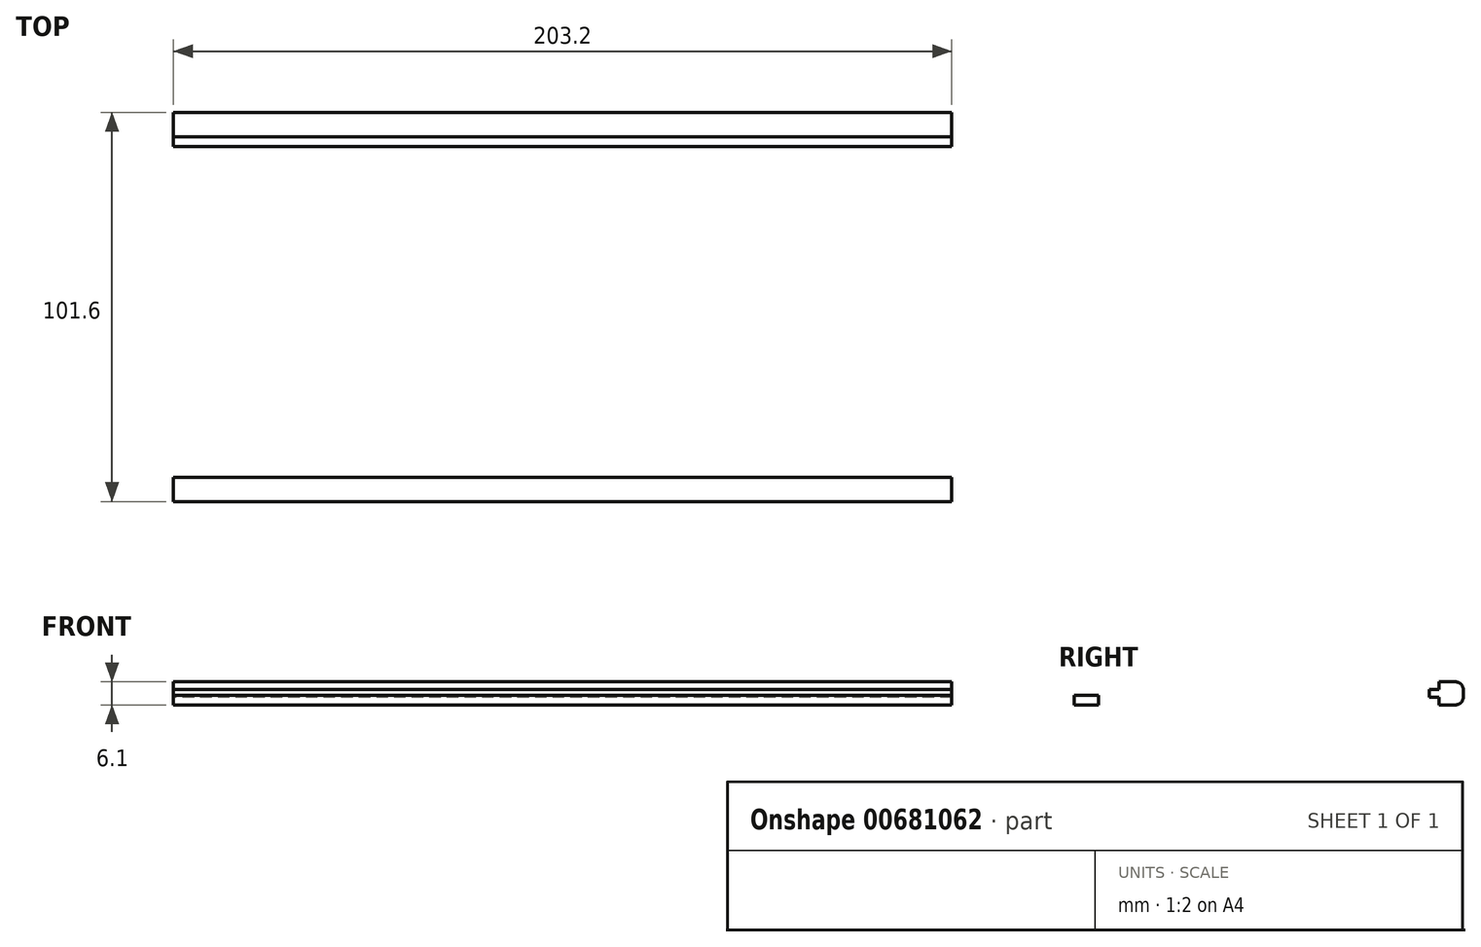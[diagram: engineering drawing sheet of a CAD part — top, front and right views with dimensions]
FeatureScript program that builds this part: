
annotation { "Feature Type Name" : "Feature", "Feature Type Description" : "" }
export const myFeature = defineFeature(function(context is Context, id is Id, definition is map)
    precondition{}
    {
        {
            var Q0;
            Q0=qCreatedBy(makeId("Top.planeOp"),FACE);
            var sketch = newSketch(context, id + "F0", { "sketchPlane" : qUnion([Q0])});
            skLineSegment(sketch, "E0", {"start": v(0, 0) * mm, "end": v(-71.71, 0) * mm});
            skLineSegment(sketch, "E1", {"start": v(71.71, 0) * mm, "end": v(0, 0) * mm});
            skLineSegment(sketch, "E2.bottom", {"start": v(-106, 53.84) * mm, "end": v(97.2, 53.84) * mm});
            skLineSegment(sketch, "E2.top", {"start": v(-106, -47.76) * mm, "end": v(97.2, -47.76) * mm});
            skLineSegment(sketch, "E2.left", {"start": v(-106, 53.84) * mm, "end": v(-106, -47.76) * mm});
            skLineSegment(sketch, "E2.right", {"start": v(97.2, 53.84) * mm, "end": v(97.2, -47.76) * mm});
            skLineSegment(sketch, "E3.top", {"start": v(-106, -41.41) * mm, "end": v(97.2, -41.41) * mm});
            skLineSegment(sketch, "E3.left", {"start": v(-106, -47.76) * mm, "end": v(-106, -41.41) * mm});
            skLineSegment(sketch, "E3.right", {"start": v(97.2, -47.76) * mm, "end": v(97.2, -41.41) * mm});
            skLineSegment(sketch, "E4.top", {"start": v(-106, 47.49) * mm, "end": v(97.2, 47.49) * mm});
            skLineSegment(sketch, "E4.left", {"start": v(-106, 53.84) * mm, "end": v(-106, 47.49) * mm});
            skLineSegment(sketch, "E4.right", {"start": v(97.2, 53.84) * mm, "end": v(97.2, 47.49) * mm});
            skText(sketch, "E5", { "text": "Kira\n", "fontName": "OpenSans-Regular.ttf"});
            const initialGuessF0  = {"E5": [-0.0568, -0.01355, 1, 0, 0.04053]};
            skSetInitialGuess(sketch, initialGuessF0);
            skSolve(sketch);
        }
        {
            var Q0;
            Q0=makeQuery(id+"F0.imprint","IMPRINT",FACE,{"disambiguationData":[TD([[makeQuery(id+"F0.imprint","IMPRINT",EDGE,{"derivedFrom":sQuery(id+"F0.wireOp",EDGE,"E2.bottom")}),-1.0]])]});
            var Q1;
            Q1=makeQuery(id+"F0.imprint","IMPRINT",FACE,{"disambiguationData":[TD([[makeQuery(id+"F0.imprint","IMPRINT",EDGE,{"derivedFrom":sQuery(id+"F0.wireOp",EDGE,"E2.top")}),1.0]])]});
            extrude(context, id + "F1", {"entities" : qUnion([Q0, Q1]), "depth" : 6.1 * mm, "offsetDistance" : 25.4 * mm});
        }
        {
            var Q0;
            Q0=makeQuery(id+"F0.imprint","IMPRINT",FACE,{"disambiguationData":[TD([[makeQuery(id+"F0.imprint","IMPRINT",EDGE,{"derivedFrom":sQuery(id+"F0.wireOp",EDGE,"E2.left")}),1.0]])]});
            extrude(context, id + "F2", {"entities" : qUnion([Q0]), "depth" : 2.54 * mm, "offsetDistance" : 25.4 * mm});
        }
        {
            var Q0;
            Q0=makeQuery(id+"F1.opExtrude","SWEPT_FACE",FACE,{"disambiguationData":[OSD([sQuery(id+"F0.wireOp",EDGE,"E4.top")])]});
            var sketch = newSketch(context, id + "F3", { "sketchPlane" : qUnion([Q0])});
            skLineSegment(sketch, "E6", {"start": v(-106, 4) * mm, "end": v(97.2, 4) * mm});
            skLineSegment(sketch, "E7", {"start": v(97.2, 4) * mm, "end": v(97.2, 2.04) * mm});
            skLineSegment(sketch, "E8", {"start": v(97.2, 2.04) * mm, "end": v(-48.8, 2.04) * mm});
            skLineSegment(sketch, "E9", {"start": v(-48.8, 2.04) * mm, "end": v(-106, 2.04) * mm});
            skLineSegment(sketch, "E10", {"start": v(-106, 2.04) * mm, "end": v(-106, 4) * mm});
            skSolve(sketch);
        }
        {
            var Q0;
            Q0=makeQuery(id+"F3.imprint","IMPRINT",FACE,{"disambiguationData":[TD([[makeQuery(id+"F3.imprint","IMPRINT",EDGE,{"derivedFrom":sQuery(id+"F3.wireOp",EDGE,"E6")}),-1.0]])]});
            extrude(context, id + "F4", {"entities" : qUnion([Q0]), "operationType" : NewBodyOperationType.ADD, "depth" : 2.54 * mm, "offsetDistance" : 25.4 * mm});
        }
        {
            var Q0;
            Q0=makeQuery(id+"F1.opExtrude","CAP_EDGE",EDGE,{"disambiguationData":[OSD([sQuery(id+"F0.wireOp",EDGE,"E2.top")])],"isStart":false});
            var Q1;
            Q1=makeQuery(id+"F1.opExtrude","CAP_EDGE",EDGE,{"disambiguationData":[OSD([sQuery(id+"F0.wireOp",EDGE,"E2.top")])],"isStart":true});
            var Q2;
            Q2=makeQuery(id+"F1.opExtrude","CAP_EDGE",EDGE,{"disambiguationData":[OSD([sQuery(id+"F0.wireOp",EDGE,"E2.bottom")])],"isStart":false});
            var Q3;
            Q3=makeQuery(id+"F1.opExtrude","CAP_EDGE",EDGE,{"disambiguationData":[OSD([sQuery(id+"F0.wireOp",EDGE,"E2.bottom")])],"isStart":true});
            fillet(context, id + "F5", {"entities" : qUnion([Q0, Q1, Q2, Q3]), "radius" : 2.54 * mm, "tangentPropagation" : true, "rho" : 0.5, "crossSection" : FilletCrossSection.CONIC, "allowEdgeOverflow" : false});
        }
    });
